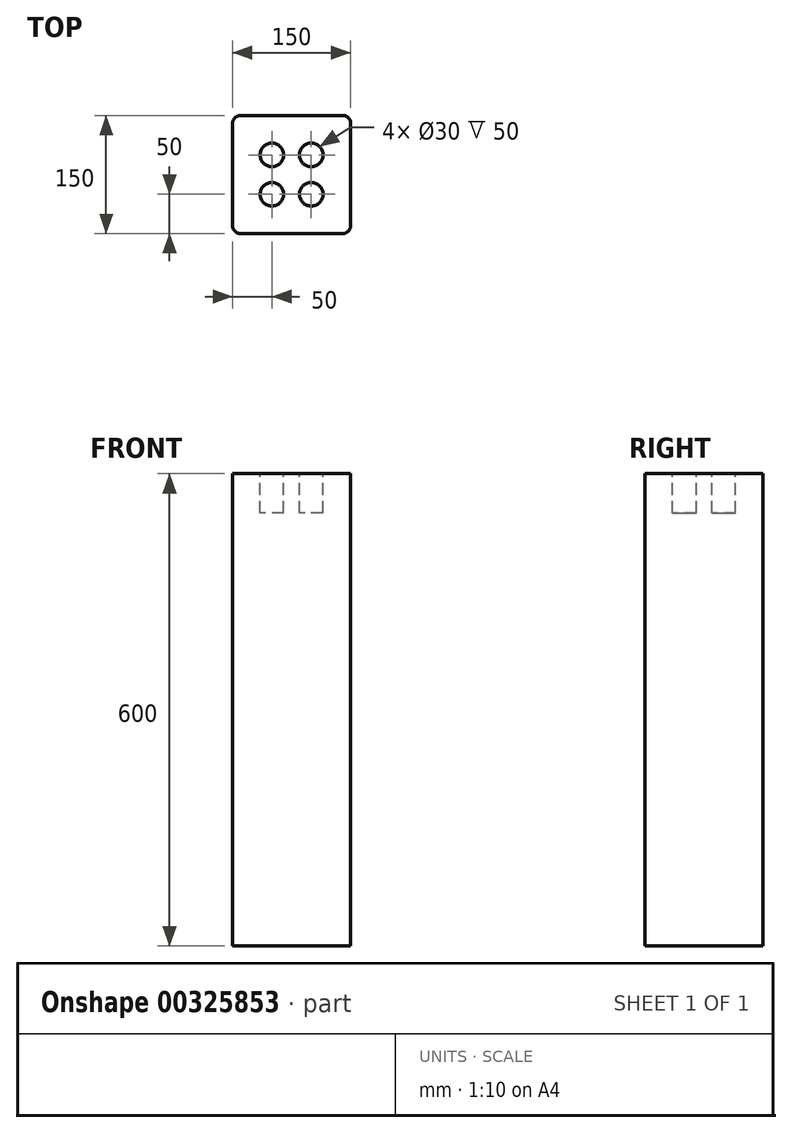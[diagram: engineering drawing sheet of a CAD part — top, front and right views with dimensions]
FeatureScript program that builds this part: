
annotation { "Feature Type Name" : "Feature", "Feature Type Description" : "" }
export const myFeature = defineFeature(function(context is Context, id is Id, definition is map)
    precondition{}
    {
        {
            var Q0;
            Q0=qCreatedBy(makeId("Top.planeOp"),FACE);
            var sketch = newSketch(context, id + "F0", { "sketchPlane" : qUnion([Q0])});
            skLineSegment(sketch, "E0.bottom", {"start": v(0, 0) * mm, "end": v(150, 0) * mm});
            skLineSegment(sketch, "E0.top", {"start": v(0, 150) * mm, "end": v(150, 150) * mm});
            skLineSegment(sketch, "E0.left", {"start": v(0, 0) * mm, "end": v(0, 150) * mm});
            skLineSegment(sketch, "E0.right", {"start": v(150, 0) * mm, "end": v(150, 150) * mm});
            skSolve(sketch);
        }
        {
            var Q0;
            Q0 = qSketchRegion(id + "F0", true);
            extrude(context, id + "F1", {"entities" : qUnion([Q0]), "depth" : 600 * mm});
        }
        {
            var Q0;
            Q0=makeQuery(id+"F1.opExtrude","SWEPT_EDGE",EDGE,{"disambiguationData":[OSD([sQuery(id+"F0.wireOp",EDGE,"E0.top"),sQuery(id+"F0.wireOp",EDGE,"E0.left")])]});
            var Q1;
            Q1=makeQuery(id+"F1.opExtrude","SWEPT_EDGE",EDGE,{"disambiguationData":[OSD([sQuery(id+"F0.wireOp",EDGE,"E0.top"),sQuery(id+"F0.wireOp",EDGE,"E0.right")])]});
            var Q2;
            Q2=makeQuery(id+"F1.opExtrude","SWEPT_EDGE",EDGE,{"disambiguationData":[OSD([sQuery(id+"F0.wireOp",EDGE,"E0.bottom"),sQuery(id+"F0.wireOp",EDGE,"E0.right")])]});
            var Q3;
            Q3=makeQuery(id+"F1.opExtrude","SWEPT_EDGE",EDGE,{"disambiguationData":[OSD([sQuery(id+"F0.wireOp",EDGE,"E0.bottom"),sQuery(id+"F0.wireOp",EDGE,"E0.left")])]});
            fillet(context, id + "F2", {"entities" : qUnion([Q0, Q1, Q2, Q3]), "radius" : 10 * mm, "tangentPropagation" : true, "allowEdgeOverflow" : false});
        }
        {
            var Q0;
            Q0=makeQuery(id+"F1.opExtrude","CAP_FACE",FACE,{"disambiguationData":[OSD([sQuery(id+"F0.wireOp",EDGE,"E0.bottom"),sQuery(id+"F0.wireOp",EDGE,"E0.top"),sQuery(id+"F0.wireOp",EDGE,"E0.left"),sQuery(id+"F0.wireOp",EDGE,"E0.right")])],"isStart":false});
            var sketch = newSketch(context, id + "F3", { "sketchPlane" : qUnion([Q0])});
            skCircle(sketch, "E1", {"center": v(50, 100) * mm, "radius": 15 * mm});
            skCircle(sketch, "E2", {"center": v(100, 100) * mm, "radius": 15 * mm});
            skCircle(sketch, "E3", {"center": v(100, 50) * mm, "radius": 15 * mm});
            skCircle(sketch, "E4", {"center": v(50, 50) * mm, "radius": 15 * mm});
            skSolve(sketch);
        }
        {
            var Q0;
            Q0 = qSketchRegion(id + "F3", true);
            extrude(context, id + "F4", {"entities" : qUnion([Q0]), "operationType" : NewBodyOperationType.REMOVE, "oppositeDirection" : true, "depth" : 50 * mm});
        }
    });
